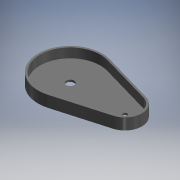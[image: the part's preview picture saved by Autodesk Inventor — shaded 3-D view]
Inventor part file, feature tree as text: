
AUTODESK INVENTOR PART (.ipt)
format: ipt  version: 2019 (Build 230136000, 136)  size: 123,392 bytes
history: native  units: mm (DEFAULTED — no unit token found)
features: sketch x4, extrude x2, hole x2
ambient origin geometry x8: Origin, YZ Plane, XZ Plane, XY Plane, X Axis, Y Axis, Z Axis, Center Point
bodies: Solid1 (feature_tree)
feature tree (8):
  extrude  "Extrusion1"  Depth=57.15mm
  sketch  "Sketch3"  dims[d2=92.202mm d3=0.0mm]
  sketch  "Sketch4"  dims[d4=3.175mm d5=0.0mm]
  hole  "Hole1"  [1 undecoded]
  hole  "Hole2"  [1 undecoded]
  extrude  "Extrusion2"  Depth=50.8mm
  sketch  "Sketch1"  dims[d0=107.95mm d1=57.15mm]
  sketch  "Sketch5"  dims[d6=13.208mm d7=7.5mm d8=3.75mm d9=2.5mm d10=90.0deg d11=10.0mm d12=20.594885mm d13=7.112mm d14=7.5mm d15=3.75mm d16=2.5mm d17=90.0deg d18=10.0mm d19=20.594885mm d20=101.6mm d21=50.8mm d22=15.875mm d23=0.0mm]
note: 2 required parameter values undecoded (feature->parameter linkage not recoverable at this tier; creation-order binding heuristic only, values carry confidence <= 0.55)
